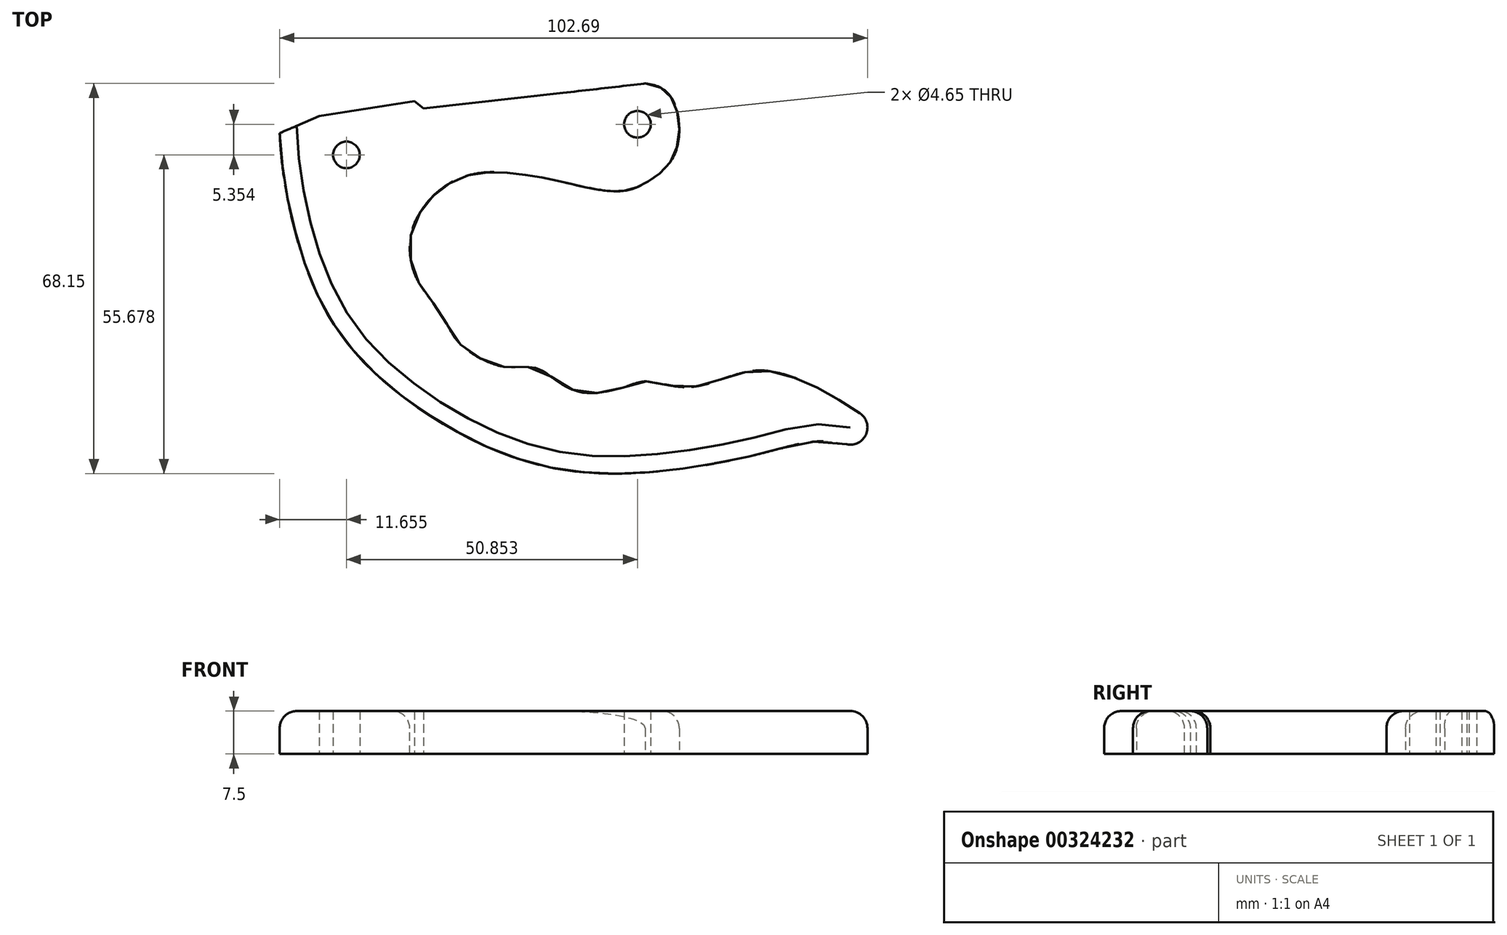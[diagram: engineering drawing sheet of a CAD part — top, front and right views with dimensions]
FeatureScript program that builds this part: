
annotation { "Feature Type Name" : "Feature", "Feature Type Description" : "" }
export const myFeature = defineFeature(function(context is Context, id is Id, definition is map)
    precondition{}
    {
        {
            var Q0;
            Q0=qCreatedBy(makeId("Top.planeOp"),FACE);
            var sketch = newSketch(context, id + "F0", { "sketchPlane" : qUnion([Q0])});
            skLineSegment(sketch, "E0", {"start": v(-52.85, 50.78) * mm, "end": v(-36.2, 53.4) * mm});
            skLineSegment(sketch, "E1", {"start": v(-36.2, 53.4) * mm, "end": v(-34.61, 52.09) * mm});
            skLineSegment(sketch, "E2", {"start": v(-34.61, 52.09) * mm, "end": v(4.12, 56.46) * mm});
            skFitSpline(sketch, "E3", {"points": [v(-59.76, 47.8) * mm, v(-55.17, 24.48) * mm, v(-44.22, 6.93) * mm, v(-16.82, -9.53) * mm, v(8.63, -11.05) * mm, v(26.1, -7.74) * mm, v(37.36, -6.22) * mm, v(46.18, -6.4) * mm], "startDerivative": vector(5.53, -143.4) * mm, "endDerivative": vector(33.06, 63.74) * mm});
            skFitSpline(sketch, "E4", {"points": [v(46.18, -6.4) * mm, v(42.7, -1.92) * mm, v(32.75, 4) * mm, v(25.66, 6.23) * mm, v(21.98, 6.1) * mm, v(18, 4.96) * mm, v(12.23, 3.46) * mm, v(7.23, 3.96) * mm, v(4.07, 4.4) * mm, v(0.11, 3.33) * mm, v(-6.37, 2.41) * mm, v(-11.29, 4.47) * mm, v(-15.06, 6.74) * mm, v(-19.65, 6.82) * mm, v(-25.7, 9) * mm, v(-29.26, 12.18) * mm, v(-31.7, 16.5) * mm, v(-35.41, 21.52) * mm, v(-36.64, 30.83) * mm, v(-28.62, 39.78) * mm, v(-17.79, 40.65) * mm, v(-10.12, 39.2) * mm, v(-4.45, 37.99) * mm, v(0.6, 37.74) * mm, v(4.94, 39.53) * mm, v(9.34, 44.35) * mm, v(9.14, 53.13) * mm, v(4.12, 56.46) * mm], "startDerivative": vector(48.47, 120.72) * mm, "endDerivative": vector(-210.65, 20.45) * mm});
            skLineSegment(sketch, "E5", {"start": v(-52.85, 50.78) * mm, "end": v(-59.76, 47.8) * mm});
            skFitSpline(sketch, "E6", {"points": [v(46.18, -6.4) * mm, v(42.7, -1.92) * mm, v(32.75, 4) * mm, v(25.66, 6.23) * mm, v(21.98, 6.1) * mm, v(18, 4.96) * mm, v(12.23, 3.46) * mm, v(7.23, 3.96) * mm, v(4.07, 4.4) * mm, v(0.11, 3.33) * mm, v(-6.37, 2.41) * mm, v(-11.29, 4.47) * mm, v(-15.06, 6.74) * mm, v(-19.65, 6.82) * mm, v(-25.7, 9) * mm, v(-29.26, 12.18) * mm, v(-31.7, 16.5) * mm, v(-35.41, 21.52) * mm, v(-36.64, 30.83) * mm, v(-28.62, 39.78) * mm, v(-17.79, 40.65) * mm, v(-10.12, 39.2) * mm, v(-4.45, 37.99) * mm, v(0.6, 37.74) * mm, v(4.94, 39.53) * mm, v(9.34, 44.35) * mm, v(9.14, 53.13) * mm, v(4.12, 56.46) * mm], "startDerivative": vector(48.47, 120.72) * mm, "endDerivative": vector(-210.65, 20.45) * mm});
            skPoint(sketch, "E7", {"position": v(-45.97, 44.2) * mm});
            skPoint(sketch, "E8", {"position": v(0.6, 49.1) * mm});
            skPoint(sketch, "E9", {"position": v(-37.04, 27.3) * mm});
            skPoint(sketch, "E10", {"position": v(-37.24, 26.74) * mm});
            skSolve(sketch);
        }
        {
            var Q0;
            Q0=makeQuery(id+"F0.imprint","IMPRINT",FACE,{"disambiguationData":[TD([[makeQuery(id+"F0.imprint","IMPRINT",EDGE,{"derivedFrom":sQuery(id+"F0.wireOp",EDGE,"E0")}),-1.0]])]});
            extrude(context, id + "F1", {"entities" : qUnion([Q0]), "depth" : 7.5 * mm});
        }
        {
            var Q0;
            Q0=makeQuery(id+"F1.opExtrude","CAP_EDGE",EDGE,{"disambiguationData":[OSD([sQuery(id+"F0.wireOp",EDGE,"E4"),sQuery(id+"F0.wireOp",EDGE,"E6")])],"isStart":false});
            var Q1;
            Q1=makeQuery(id+"F1.opExtrude","CAP_EDGE",EDGE,{"disambiguationData":[OSD([sQuery(id+"F0.wireOp",EDGE,"E3")])],"isStart":false});
            var Q2;
            Q2=makeQuery(id+"F1.opExtrude","SWEPT_EDGE",EDGE,{"disambiguationData":[OSD([sQuery(id+"F0.wireOp",EDGE,"E3"),sQuery(id+"F0.wireOp",EDGE,"E4")])]});
            fillet(context, id + "F2", {"entities" : qUnion([Q0, Q1, Q2]), "radius" : 3 * mm, "allowEdgeOverflow" : false});
        }
        {
            var Q0;
            Q0=makeQuery(id+"F1.opExtrude","CAP_FACE",FACE,{"disambiguationData":[OSD([sQuery(id+"F0.wireOp",EDGE,"E0"),sQuery(id+"F0.wireOp",EDGE,"E1"),sQuery(id+"F0.wireOp",EDGE,"E2"),sQuery(id+"F0.wireOp",EDGE,"E3"),sQuery(id+"F0.wireOp",EDGE,"E4"),sQuery(id+"F0.wireOp",EDGE,"E5"),sQuery(id+"F0.wireOp",EDGE,"E6")])],"isStart":true});
            var sketch = newSketch(context, id + "F3", { "sketchPlane" : qUnion([Q0])});
            skCircle(sketch, "E11", {"center": v(2.75, -49.34) * mm, "radius": 2.33 * mm});
            skPoint(sketch, "E11.first.point", {"position": v(1.9, -47.18) * mm});
            skPoint(sketch, "E11.second.point", {"position": v(0.54, -50.07) * mm});
            skPoint(sketch, "E11.third.point", {"position": v(3.74, -51.44) * mm});
            skCircle(sketch, "E12", {"center": v(-48.1, -43.99) * mm, "radius": 2.33 * mm});
            skPoint(sketch, "E12.first.point", {"position": v(-47.06, -46.06) * mm});
            skPoint(sketch, "E12.second.point", {"position": v(-46.57, -45.73) * mm});
            skPoint(sketch, "E12.third.point", {"position": v(-47.75, -46.28) * mm});
            skSolve(sketch);
        }
        {
            var Q0;
            Q0=makeQuery(id+"F3.imprint","IMPRINT",FACE,{"disambiguationData":[TD([[makeQuery(id+"F3.imprint","IMPRINT",EDGE,{"derivedFrom":sQuery(id+"F3.wireOp",EDGE,"E12")}),1.0]])]});
            var Q1;
            Q1=makeQuery(id+"F3.imprint","IMPRINT",FACE,{"disambiguationData":[TD([[makeQuery(id+"F3.imprint","IMPRINT",EDGE,{"derivedFrom":sQuery(id+"F3.wireOp",EDGE,"E11")}),1.0]])]});
            var Q2;
            Q2=sQuery(id+"F3.wireOp",EDGE,"E11");
            extrude(context, id + "F4", {"entities" : qUnion([Q0, Q1]), "operationType" : NewBodyOperationType.REMOVE, "surfaceEntities" : qUnion([Q2]), "endBound" : BoundingType.THROUGH_ALL, "oppositeDirection" : true, "depth" : 17.3 * mm});
        }
    });
